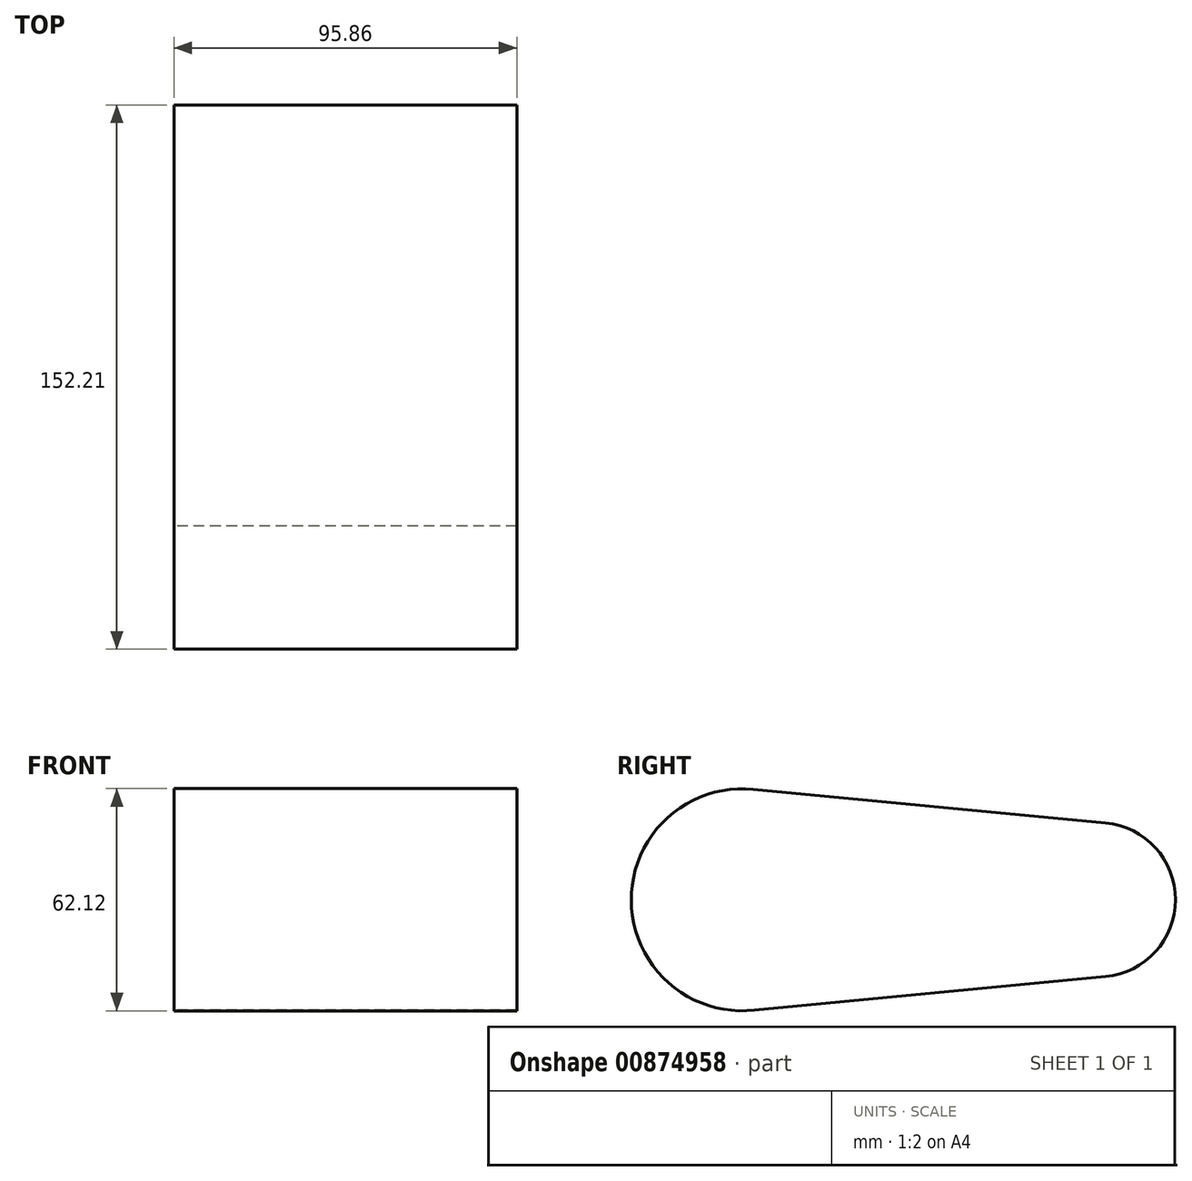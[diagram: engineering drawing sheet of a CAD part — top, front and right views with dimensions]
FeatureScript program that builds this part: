
annotation { "Feature Type Name" : "Feature", "Feature Type Description" : "" }
export const myFeature = defineFeature(function(context is Context, id is Id, definition is map)
    precondition{}
    {
        {
            var Q0;
            Q0=qCreatedBy(makeId("Right.planeOp"),FACE);
            var sketch = newSketch(context, id + "F0", { "sketchPlane" : qUnion([Q0])});
            skCircle(sketch, "E0", {"center": v(-50.02, 0) * mm, "radius": 31.06 * mm});
            skCircle(sketch, "E1", {"center": v(49.52, 0) * mm, "radius": 21.61 * mm});
            skLineSegment(sketch, "E2", {"start": v(-46.56, -30.87) * mm, "end": v(51.57, -21.51) * mm});
            skLineSegment(sketch, "E3", {"start": v(-47.18, 30.93) * mm, "end": v(51.57, 21.51) * mm});
            skSolve(sketch);
        }
        {
            var Q0;
            Q0 = qSketchRegion(id + "F0", true);
            extrude(context, id + "F1", {"entities" : qUnion([Q0]), "depth" : 25 * mm, "offsetDistance" : 25 * mm});
        }
        {
            var Q0;
            Q0=makeQuery(id+"F1.opExtrude","CAP_FACE",FACE,{"disambiguationData":[OSD([sQuery(id+"F0.wireOp",EDGE,"E0"),sQuery(id+"F0.wireOp",EDGE,"E1"),sQuery(id+"F0.wireOp",EDGE,"E2"),sQuery(id+"F0.wireOp",EDGE,"E3")])],"isStart":false});
            extrude(context, id + "F2", {"entities" : qUnion([Q0]), "operationType" : NewBodyOperationType.ADD, "depth" : 25 * mm, "offsetDistance" : 25 * mm});
        }
        {
            var Q0;
            Q0=makeQuery(id+"F1.opExtrude","CAP_FACE",FACE,{"disambiguationData":[OSD([sQuery(id+"F0.wireOp",EDGE,"E0"),sQuery(id+"F0.wireOp",EDGE,"E1"),sQuery(id+"F0.wireOp",EDGE,"E2"),sQuery(id+"F0.wireOp",EDGE,"E3")])],"isStart":true});
            extrude(context, id + "F3", {"entities" : qUnion([Q0]), "operationType" : NewBodyOperationType.ADD, "depth" : 45.86 * mm, "offsetDistance" : 25 * mm});
        }
    });
